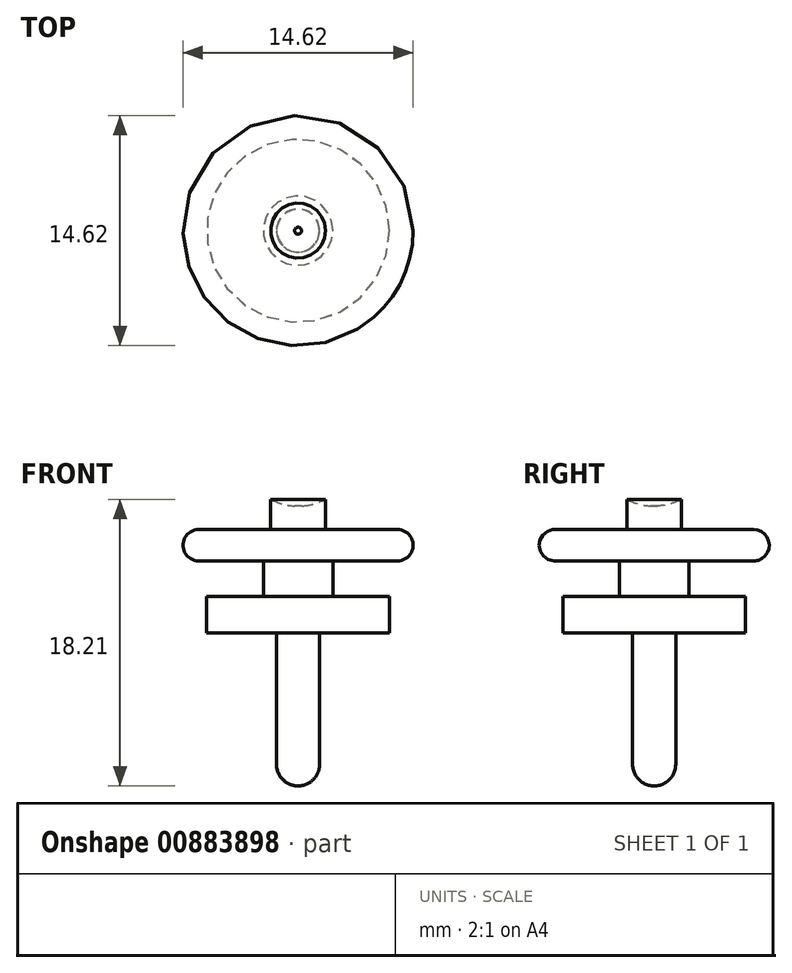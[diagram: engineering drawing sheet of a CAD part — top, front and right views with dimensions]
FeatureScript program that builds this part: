
annotation { "Feature Type Name" : "Feature", "Feature Type Description" : "" }
export const myFeature = defineFeature(function(context is Context, id is Id, definition is map)
    precondition{}
    {
        {
            var Q0;
            Q0=qCreatedBy(makeId("Front.planeOp"),FACE);
            var sketch = newSketch(context, id + "F0", { "sketchPlane" : qUnion([Q0])});
            skPoint(sketch, "E0", {"position": v(1.37, 1.37) * mm});
            skArc(sketch, "E1", {"start": v(0, 0) * mm, "mid": v(0.97, 0.4) * mm, "end": v(1.37, 1.37) * mm});
            skPoint(sketch, "E2", {"position": v(0, 0) * mm});
            skLineSegment(sketch, "E3", {"start": v(1.37, 1.37) * mm, "end": v(1.37, 9.73) * mm});
            skLineSegment(sketch, "E4", {"start": v(1.37, 9.73) * mm, "end": v(5.8, 9.73) * mm});
            skLineSegment(sketch, "E5", {"start": v(5.8, 9.73) * mm, "end": v(5.8, 12.03) * mm});
            skLineSegment(sketch, "E6", {"start": v(5.8, 12.03) * mm, "end": v(2.2, 12.03) * mm});
            skLineSegment(sketch, "E7", {"start": v(2.2, 12.03) * mm, "end": v(2.2, 14.29) * mm});
            skLineSegment(sketch, "E8", {"start": v(2.2, 14.29) * mm, "end": v(6.3, 14.29) * mm});
            skLineSegment(sketch, "E9", {"start": v(1.75, 16.29) * mm, "end": v(6.3, 16.29) * mm});
            skLineSegment(sketch, "E10", {"start": v(1.75, 16.29) * mm, "end": v(1.75, 18.21) * mm});
            skArc(sketch, "E11", {"start": v(1.75, 18.21) * mm, "mid": v(3.36, 22.05) * mm, "end": v(0, 24.52) * mm});
            skArc(sketch, "E12", {"start": v(6.3, 14.29) * mm, "mid": v(7.3, 15.29) * mm, "end": v(6.3, 16.29) * mm});
            skPoint(sketch, "E13", {"position": v(7.3, 15.29) * mm});
            skLineSegment(sketch, "E14", {"start": v(0, 24.52) * mm, "end": v(0, 0) * mm});
            skSolve(sketch);
        }
        {
            var Q0;
            Q0=makeQuery(id+"F0.imprint","IMPRINT",FACE,{"disambiguationData":[TD([[makeQuery(id+"F0.imprint","IMPRINT",EDGE,{"derivedFrom":sQuery(id+"F0.wireOp",EDGE,"E1")}),1.0]])]});
            var Q1;
            Q1=sQuery(id+"F0.wireOp",EDGE,"E14");
            revolve(context, id + "F1", {"surfaceOperationType" : NewSurfaceOperationType.NEW, "entities" : qUnion([Q0]), "axis" : qUnion([Q1]), "revolveType" : RevolveType.FULL});
        }
    });
